# Revit family: Maxlogic  Module de désenfumage adressable Intelligent (seul)
name_source: partatom
category: Fire Alarm Devices
units: mm (PartAtom-declared; Revit-internal decimal feet)

## family parameters
Cut with Voids When Loaded = No
Host = Face
Maintain Annotation Orientation = Yes
OmniClass Number = 23.85.30.21
OmniClass Title = Environmental Detection/Registration
Part Type = Normal
Room Calculation Point = No
Round Connector Dimension = Use Diameter
Shared = No

## types (6) — shared parameters
Adresse ligne 1 = Şerifali Mahallesi Kutup Sokak No:27/1-2-4 Ümraniye TR-34775 İSTANBUL
Code de Performance = EN 54-17 / EN 54-18
Couleur = Blanc
Deuxième Matèriel = Plastique
Durée de la garantie Travail = 2
Durée de la garantie de pièces rechange = 2
Hauteur Nominal = 86 mm
Largeur Nominal = 60 mm
Longeur Nominal = 158 mm
Manuel d'Installation = https://mavilielektronik.com
Manufacturer = Mavili Elektronik Ticaret A.Ş.
Matèriel Principe = Plastique Blanche ABS
Model = Maxlogic
Numéro de Fax = (+)90 216 466 45 10
Surface de Montage = Montage à Mur
Tempèrature de Fonctionnement = (-30°C) - (+60°C)
URL = https://www.mavili.com.tr
Unité de durée de garantie = Ans
Voltage de fonctionnement (défaut) = 24 V/DC
Voltage fonction d'opération = 18-33V/DC
zero-valued in all types: Cost, Default Elevation

## per-type parameters (varying)
| type | Alimentation d'externe | Charger adresse d'appareil | Code de Produit | Description |
| Maxlogic Adressable Intelligent module de désenfumage  24V DC | 24 V/DC | Appareil d'adressage à Main | ML-1356 | Adressable Intelligent module de désenfumage  24V DC |
| Maxlogic Adressable Intelligent module de désenfumage 24V DC Isolateur de Court-Circuit | 24 V/DC | Appareil d'adressage à Main | ML-1356.SCI | Adressable Intelligent module de désenfumage 24V DC Isolateur de Court-Circuit |
| Maxlogic Adressable Intelligent module de désenfumage 24V AC | 24 V/AC | Appareil d'adressage à Main | ML-1357 | Adressable Intelligent module de désenfumage  24V AC |
| Maxlogic Adressable Intelligent module de désenfumage  24V AC ,Isolateur de Court-Circuit | 24 V/AC | Appareil d'adressage à Mur | ML-1357.SCI | Adressable Intelligent module de désenfumage 24V AC,Isolateur de Court-Circuit |
| Maxlogic Adressable Intelligent module de désenfumage 220V AC | 220 V/AC | Appareil d'adressage à Main | ML-1358 | Adressable Intelligent module de désenfumage  220V AC |
| Maxlogic Adressable Intelligent module de désenfumage 220V AC,Isolateur de Court-Circuit | 220 V/AC | Appareil d'adressage à Main | ML-1358.SCI | Adressable Intelligent module de désenfumage 220V AC,Isolateur de Court-Circuit |

## geometry (parser evidence)
native form markers: Sweep x2
no freeform markers — native parametric forms only
